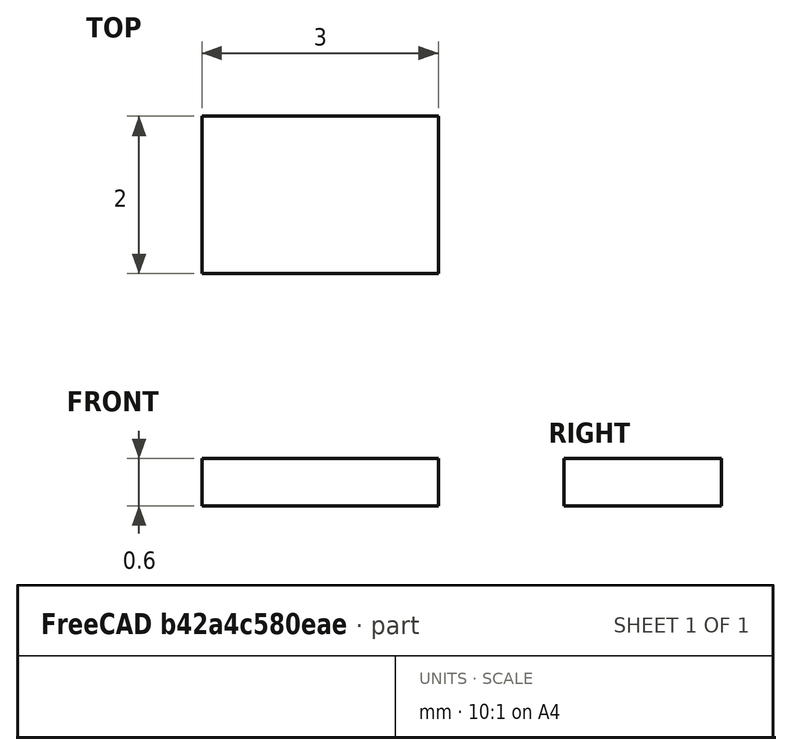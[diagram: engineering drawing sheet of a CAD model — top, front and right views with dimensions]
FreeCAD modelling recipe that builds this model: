
FCSTD DOCUMENT  (FreeCAD 0.20R29410 (Git))
Label: USON-8 (2x3mm)
License: All rights reserved
LicenseURL: http://en.wikipedia.org/wiki/All_rights_reserved
objects: Sketcher::SketchObject×1, PartDesign::Pad×1, PartDesign::Body×1
note: 4 computed .brp shape members not serialized (recipe doc carries the construction recipe); baked Part::Feature solids carry a one-line shape summary decoded from their .brp

FEATURE [Sketcher::SketchObject] Sketch
  FullyConstrained = true
  MapMode = 5
  Support = -> [XY_Plane]
  sketch-geometry (5):
    g0: LineSegment StartX=-1.5 StartY=-1 StartZ=0 EndX=-1.5 EndY=1 EndZ=0
    g1: LineSegment StartX=-1.5 StartY=1 StartZ=0 EndX=1.5 EndY=1 EndZ=0
    g2: LineSegment StartX=1.5 StartY=1 StartZ=0 EndX=1.5 EndY=-1 EndZ=0
    g3: LineSegment StartX=1.5 StartY=-1 StartZ=0 EndX=-1.5 EndY=-1 EndZ=0
    g4: GeomPoint X=0 Y=0 Z=0
  constraints (12):
    c: Coincident(g0,g1)
    c: Coincident(g1,g2)
    c: Coincident(g2,g3)
    c: Coincident(g3,g0)
    c: Horizontal(g1)
    c: Horizontal(g3)
    c: Vertical(g0)
    c: Vertical(g2)
    c: Symmetric(g1,g0,g4)
    c: Coincident(g4,g-1)
    c: DistanceY(g0,g0) = 2
    c: DistanceX(g1,g1) = 3
FEATURE [PartDesign::Pad] Pad
  Direction = (0,0,1)
  Length = 0.6
  Length2 = 10
  Profile = -> Sketch
  ReferenceAxis = -> Sketch [N_Axis]
  Type = 0
FEATURE [PartDesign::Body] Body
  Group = -> [Sketch,Pad]
  Origin = -> Origin
  Tip = -> Pad
